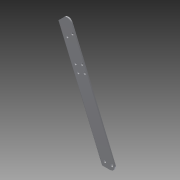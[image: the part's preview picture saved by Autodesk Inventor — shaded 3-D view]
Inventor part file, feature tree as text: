
AUTODESK INVENTOR PART (.ipt)
format: ipt  version: 2014 SP1 (Build 180222100, 222)  size: 161,792 bytes
history: native  units: in
note: dims shown in document units (in); Inventor stores cm internally (conversion verified against a paired STEP export)
features: other x3, sketch x1
ambient origin geometry x8: Origin, YZ Plane, XZ Plane, XY Plane, X Axis, Y Axis, Z Axis, Center Point
bodies: Solid1 (feature_tree)
feature tree (4):
  other  "V5 Shooter Frame Side Connector P3.ipt"
  other  "Solid1::V5 Shooter Frame Side Connector P3.ipt"
  sketch  "Sketch1"  dims[d0=0.3937in]
  other  "TaggingFeature1"
